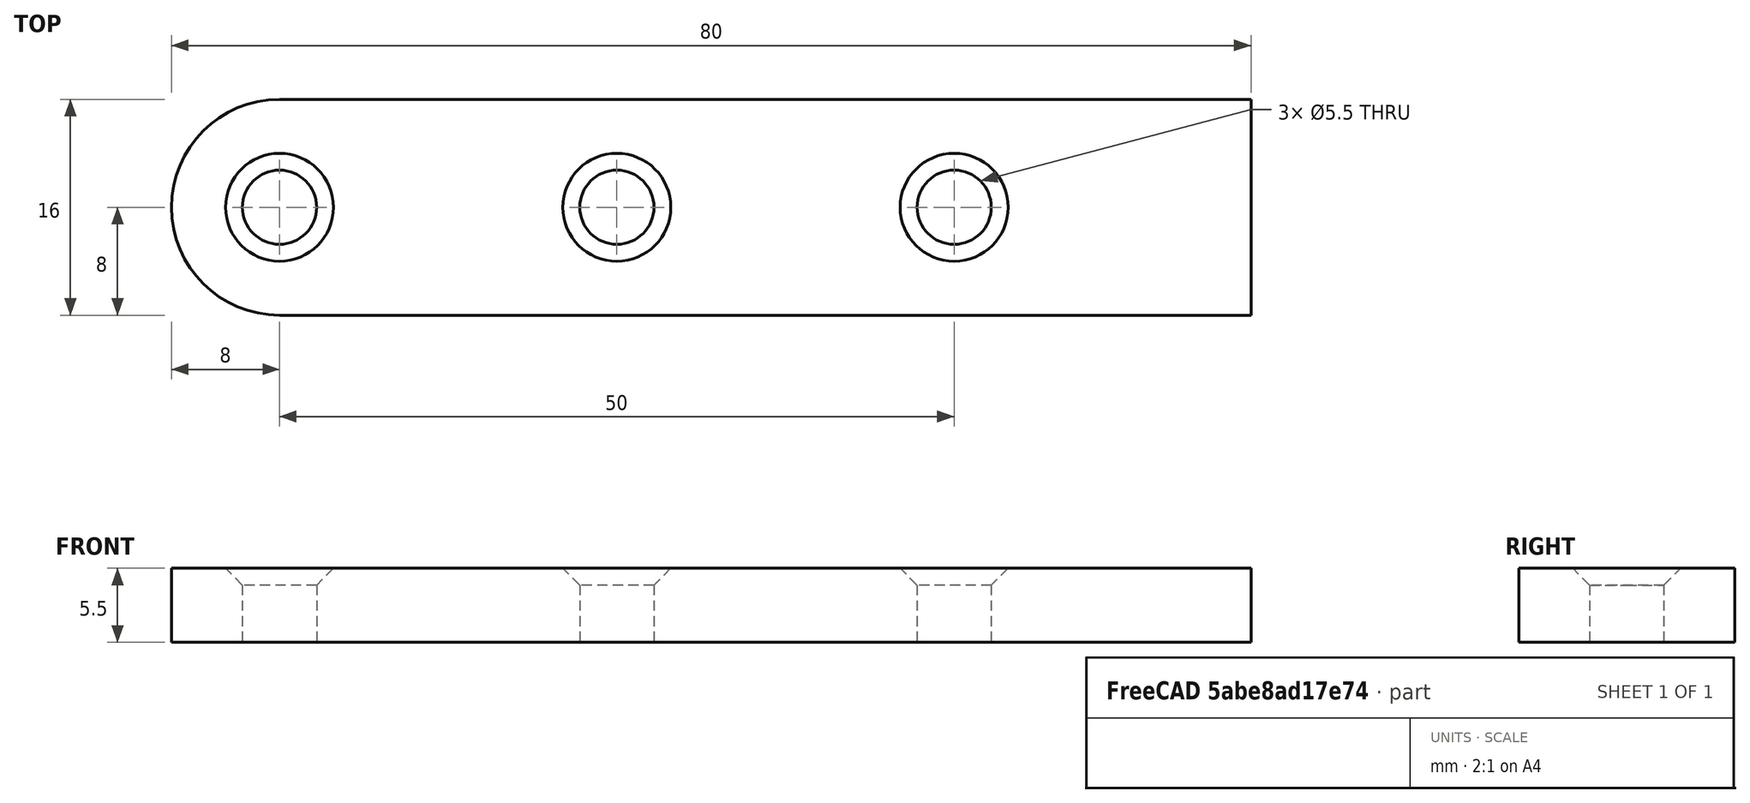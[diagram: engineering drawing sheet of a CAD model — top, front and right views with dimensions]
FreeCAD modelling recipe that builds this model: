
FCSTD DOCUMENT  (FreeCAD 0.19R24267 +99 (Git))
Label: add_pivot
License: All rights reserved
LicenseURL: http://en.wikipedia.org/wiki/All_rights_reserved
objects: Sketcher::SketchObject×4, PartDesign::Pad×2, PartDesign::Hole×2, PartDesign::Body×2, Mesh::Feature×2
note: 14 computed .brp shape members not serialized (recipe doc carries the construction recipe); baked Part::Feature solids carry a one-line shape summary decoded from their .brp

FEATURE [Sketcher::SketchObject] Sketch
  FullyConstrained = true
  MapMode = 5
  Support = -> [XY_Plane]
  sketch-geometry (4):
    g0: LineSegment StartX=5e-16 StartY=8 StartZ=0 EndX=72 EndY=8 EndZ=0
    g1: LineSegment StartX=72 StartY=8 StartZ=0 EndX=72 EndY=-8 EndZ=0
    g2: LineSegment StartX=72 StartY=-8 StartZ=0 EndX=0 EndY=-8 EndZ=0
    g3: ArcOfCircle CenterX=0 CenterY=0 CenterZ=0 NormalX=0 NormalY=0 NormalZ=1 AngleXU=0 Radius=8 StartAngle=1.5708 EndAngle=4.71239
  constraints (12):
    c: PointOnObject(g0,g-2)
    c: Horizontal(g0)
    c: Coincident(g0,g1)
    c: Vertical(g1)
    c: Coincident(g1,g2)
    c: PointOnObject(g2,g-2)
    c: Horizontal(g2)
    c: DistanceX(g0,g0) = 72
    c: DistanceY(g1,g1) = 16
    c: Coincident(g3,g-1)
    c: Coincident(g3,g0)
    c: Coincident(g3,g2)
FEATURE [PartDesign::Pad] Pad
  Direction = (1,1,1)
  Length = 5.5
  Length2 = 100
  Profile = -> Sketch
  Type = 0
FEATURE [Sketcher::SketchObject] Sketch001
  FullyConstrained = false
  MapMode = 5
  Placement = pos=(0,0,5.5) rot=(0,0,1;0rad)
  Support = -> [Pad]
  sketch-geometry (3):
    g0: Circle CenterX=0 CenterY=0 CenterZ=0 NormalX=0 NormalY=0 NormalZ=1 AngleXU=0 Radius=4
    g1: Circle CenterX=25 CenterY=0 CenterZ=0 NormalX=0 NormalY=0 NormalZ=1 AngleXU=0 Radius=4
    g2: Circle CenterX=50 CenterY=0 CenterZ=0 NormalX=0 NormalY=0 NormalZ=1 AngleXU=0 Radius=4
  constraints (7):
    c: Coincident(g0,g-1)
    c: Diameter(g0) = 8
    c: Equal(g0,g1) = 8
    c: PointOnObject(g1,g-1)
    c: DistanceX(g0,g1) = 25
    c: PointOnObject(g2,g-1)
    c: DistanceX(g1,g2) = 25
FEATURE [PartDesign::Hole] Hole
  BaseFeature = -> Pad
  Depth = 25
  DepthType = 1
  Diameter = 5.5
  DrillForDepth = false
  DrillPoint = 1
  DrillPointAngle = 118
  HoleCutCountersinkAngle = 90
  HoleCutCustomValues = false
  HoleCutDepth = 5.4
  HoleCutDiameter = 8
  HoleCutType = 2
  ModelActualThread = false
  Profile = -> Sketch001
  Tapered = false
  TaperedAngle = 111
  ThreadAngle = 60
  ThreadClass = 0
  ThreadCutOffInner = 0.0866025
  ThreadCutOffOuter = 0.173205
  ThreadDirection = 0
  ThreadFit = 0
  ThreadPitch = 0.8
  ThreadSize = 13
  ThreadType = 1
  Threaded = false
FEATURE [PartDesign::Body] Body
  Group = -> [Sketch,Pad,Sketch001,Hole]
  Origin = -> Origin
  Tip = -> Hole
FEATURE [Mesh::Feature] Mesh  label="add1"
FEATURE [Sketcher::SketchObject] Sketch002
  FullyConstrained = true
  MapMode = 5
  Support = -> [XY_Plane001]
  sketch-geometry (4):
    g0: LineSegment StartX=5e-16 StartY=8 StartZ=0 EndX=72 EndY=8 EndZ=0
    g1: LineSegment StartX=72 StartY=8 StartZ=0 EndX=72 EndY=-8 EndZ=0
    g2: LineSegment StartX=72 StartY=-8 StartZ=0 EndX=0 EndY=-8 EndZ=0
    g3: ArcOfCircle CenterX=0 CenterY=0 CenterZ=0 NormalX=0 NormalY=0 NormalZ=1 AngleXU=0 Radius=8 StartAngle=1.5708 EndAngle=4.71239
  constraints (12):
    c: PointOnObject(g0,g-2)
    c: Horizontal(g0)
    c: Coincident(g0,g1)
    c: Vertical(g1)
    c: Coincident(g1,g2)
    c: PointOnObject(g2,g-2)
    c: Horizontal(g2)
    c: DistanceX(g0,g0) = 72
    c: DistanceY(g1,g1) = 16
    c: Coincident(g3,g-1)
    c: Coincident(g3,g0)
    c: Coincident(g3,g2)
FEATURE [PartDesign::Pad] Pad001
  Direction = (1,1,1)
  Length = 5.5
  Length2 = 100
  Profile = -> Sketch002
  Type = 0
FEATURE [Sketcher::SketchObject] Sketch003
  FullyConstrained = false
  MapMode = 5
  Placement = pos=(0,0,0) rot=(1,0,0;3.14159rad)
  Support = -> [Pad001]
  sketch-geometry (3):
    g0: Circle CenterX=0 CenterY=0 CenterZ=0 NormalX=0 NormalY=0 NormalZ=1 AngleXU=0 Radius=4
    g1: Circle CenterX=25 CenterY=0 CenterZ=0 NormalX=0 NormalY=0 NormalZ=1 AngleXU=0 Radius=4
    g2: Circle CenterX=50 CenterY=0 CenterZ=0 NormalX=0 NormalY=0 NormalZ=1 AngleXU=0 Radius=4
  constraints (7):
    c: Coincident(g0,g-1)
    c: Diameter(g0) = 8
    c: Equal(g0,g1) = 8
    c: PointOnObject(g1,g-1)
    c: DistanceX(g0,g1) = 25
    c: PointOnObject(g2,g-1)
    c: DistanceX(g1,g2) = 25
FEATURE [PartDesign::Hole] Hole001
  BaseFeature = -> Pad001
  Depth = 25
  DepthType = 1
  Diameter = 5.5
  DrillForDepth = false
  DrillPoint = 1
  DrillPointAngle = 118
  HoleCutCountersinkAngle = 90
  HoleCutCustomValues = false
  HoleCutDepth = 0
  HoleCutDiameter = 8
  HoleCutType = 2
  ModelActualThread = false
  Profile = -> Sketch003
  Tapered = false
  TaperedAngle = 90
  ThreadAngle = 0
  ThreadClass = 0
  ThreadCutOffInner = 0
  ThreadCutOffOuter = 0
  ThreadDirection = 0
  ThreadFit = 0
  ThreadPitch = 0
  ThreadSize = 13
  ThreadType = 1
  Threaded = false
FEATURE [PartDesign::Body] Body001
  Group = -> [Sketch002,Pad001,Sketch003,Hole001]
  Origin = -> Origin001
  Tip = -> Hole001
FEATURE [Mesh::Feature] Mesh001  label="add2"
